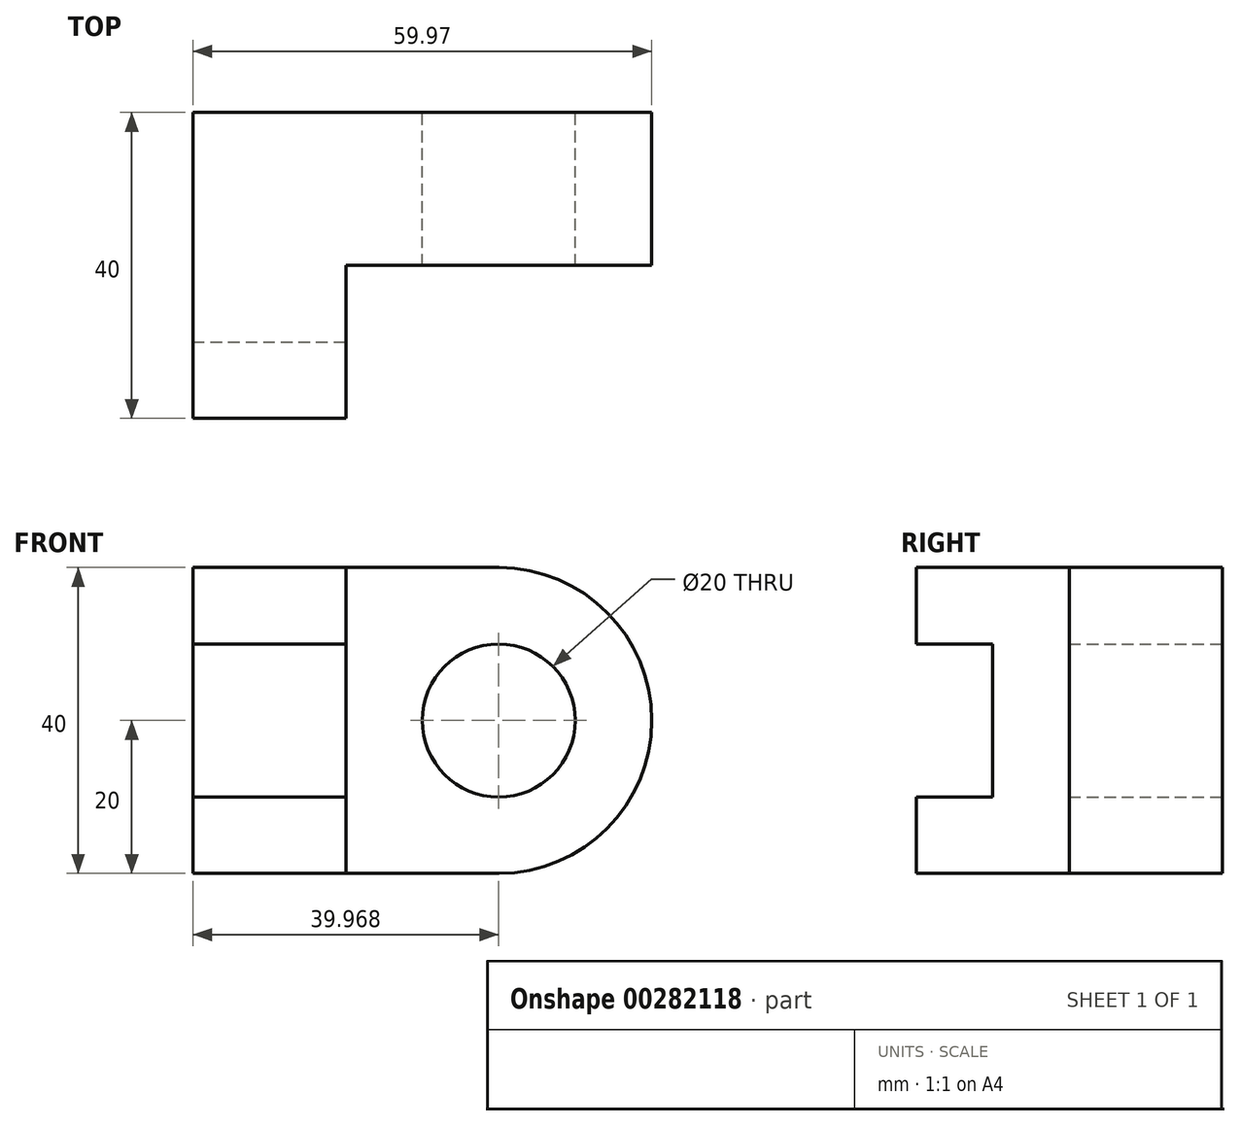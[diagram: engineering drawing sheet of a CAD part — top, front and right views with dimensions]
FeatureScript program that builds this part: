
annotation { "Feature Type Name" : "Feature", "Feature Type Description" : "" }
export const myFeature = defineFeature(function(context is Context, id is Id, definition is map)
    precondition{}
    {
        {
            var Q0;
            Q0=qCreatedBy(makeId("Front.planeOp"),FACE);
            var sketch = newSketch(context, id + "F0", { "sketchPlane" : qUnion([Q0])});
            skLineSegment(sketch, "E0", {"start": v(-40, 0) * mm, "end": v(0, 0) * mm});
            skLineSegment(sketch, "E1", {"start": v(0, 40) * mm, "end": v(-40, 40) * mm});
            skLineSegment(sketch, "E2", {"start": v(-40, 0) * mm, "end": v(-40, 40) * mm});
            skArc(sketch, "E3", {"start": v(0, 0) * mm, "mid": v(19.97, 20) * mm, "end": v(0, 40) * mm});
            skCircle(sketch, "E4", {"center": v(-0.03, 20) * mm, "radius": 10 * mm});
            skPoint(sketch, "E5.end.orphan", {"position": v(20, 40) * mm});
            skSolve(sketch);
        }
        {
            var Q0;
            Q0 = qSketchRegion(id + "F0", true);
            extrude(context, id + "F1", {"entities" : qUnion([Q0]), "depth" : 20 * mm});
        }
        {
            var Q0;
            Q0=makeQuery(id+"F1.opExtrude","CAP_FACE",FACE,{"disambiguationData":[OSD([sQuery(id+"F0.wireOp",EDGE,"E0"),sQuery(id+"F0.wireOp",EDGE,"E1"),sQuery(id+"F0.wireOp",EDGE,"E2"),sQuery(id+"F0.wireOp",EDGE,"E3"),sQuery(id+"F0.wireOp",EDGE,"E4")])],"isStart":false});
            var sketch = newSketch(context, id + "F2", { "sketchPlane" : qUnion([Q0])});
            skLineSegment(sketch, "E6", {"start": v(-40, 40) * mm, "end": v(-20, 40) * mm});
            skLineSegment(sketch, "E7", {"start": v(-20, 40) * mm, "end": v(-20, 0) * mm});
            skLineSegment(sketch, "E8", {"start": v(-20, 0) * mm, "end": v(-40, 0) * mm});
            skLineSegment(sketch, "E9", {"start": v(-40, 0) * mm, "end": v(-40, 40) * mm});
            skSolve(sketch);
        }
        {
            var Q0;
            Q0=makeQuery(id+"F2.imprint","IMPRINT",FACE,{"disambiguationData":[TD([[makeQuery(id+"F2.imprint","IMPRINT",EDGE,{"derivedFrom":sQuery(id+"F2.wireOp",EDGE,"E6")}),1.0]])]});
            extrude(context, id + "F3", {"entities" : qUnion([Q0]), "operationType" : NewBodyOperationType.ADD, "depth" : 20 * mm});
        }
        {
            var Q0;
            Q0=makeQuery(id+"F3.opExtrude","CAP_FACE",FACE,{"disambiguationData":[OSD([sQuery(id+"F2.wireOp",EDGE,"E6"),sQuery(id+"F2.wireOp",EDGE,"E7"),sQuery(id+"F2.wireOp",EDGE,"E8"),sQuery(id+"F2.wireOp",EDGE,"E9")])],"isStart":false});
            var sketch = newSketch(context, id + "F4", { "sketchPlane" : qUnion([Q0])});
            skLineSegment(sketch, "E10", {"start": v(-40, 30) * mm, "end": v(-20, 30) * mm});
            skLineSegment(sketch, "E11", {"start": v(-20, 30) * mm, "end": v(-20, 10) * mm});
            skLineSegment(sketch, "E12", {"start": v(-20, 10) * mm, "end": v(-40, 10) * mm});
            skLineSegment(sketch, "E13", {"start": v(-40, 10) * mm, "end": v(-40, 30) * mm});
            skSolve(sketch);
        }
        {
            var Q0;
            Q0 = qSketchRegion(id + "F4", true);
            extrude(context, id + "F5", {"entities" : qUnion([Q0]), "operationType" : NewBodyOperationType.REMOVE, "oppositeDirection" : true, "depth" : 10 * mm});
        }
    });
